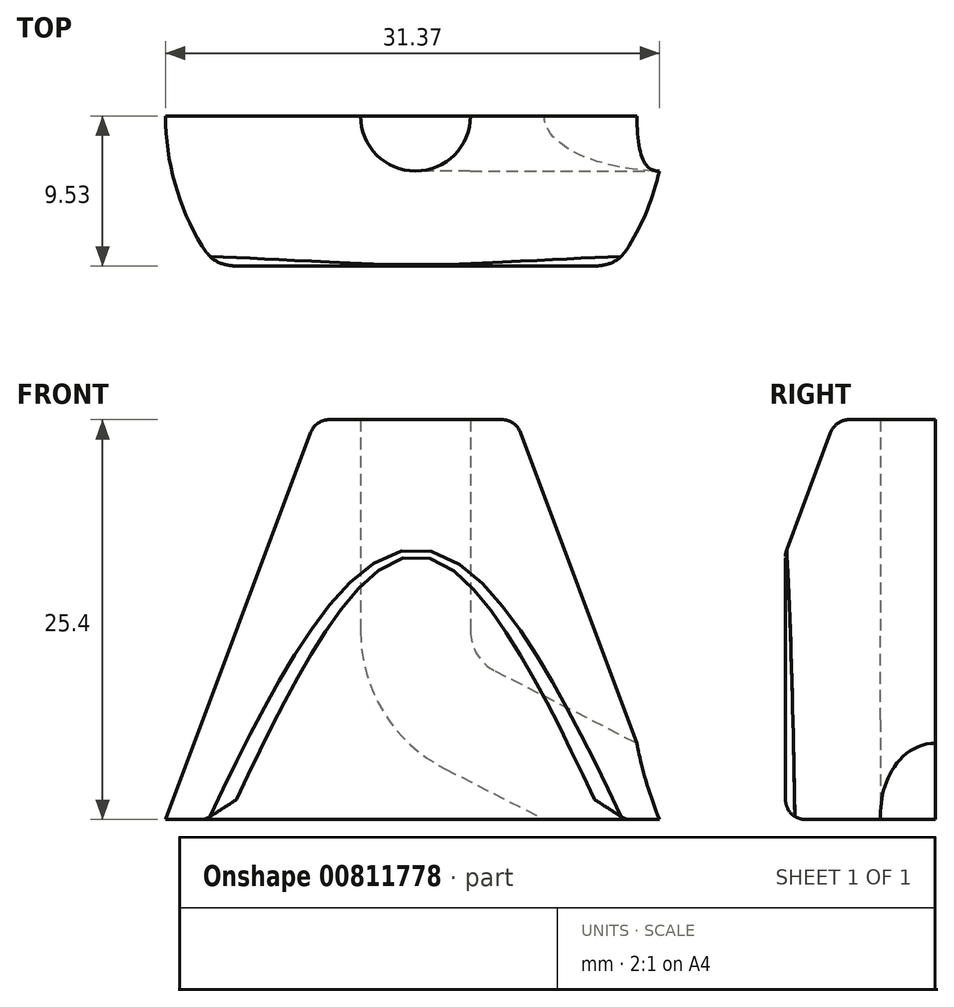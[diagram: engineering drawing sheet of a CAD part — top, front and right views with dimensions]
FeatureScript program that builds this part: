
annotation { "Feature Type Name" : "Feature", "Feature Type Description" : "" }
export const myFeature = defineFeature(function(context is Context, id is Id, definition is map)
    precondition{}
    {
        {
            var Q0;
            Q0=qCreatedBy(makeId("Front.planeOp"),FACE);
            var sketch = newSketch(context, id + "F0", { "sketchPlane" : qUnion([Q0])});
            skCircle(sketch, "E0", {"center": v(0, 0) * mm, "radius": 6.35 * mm});
            skSolve(sketch);
        }
        {
            var Q0;
            Q0=qCreatedBy(makeId("Front.planeOp"),FACE);
            cPlane(context, id + "F1", {"entities" : qUnion([Q0]), "cplaneType" : CPlaneType.OFFSET, "offset" : 25.4 * mm, "width" : 152.4 * mm, "height" : 152.4 * mm});
        }
        {
            var Q0;
            Q0=qCreatedBy(id+"F1.planeOp",FACE);
            var sketch = newSketch(context, id + "F2", { "sketchPlane" : qUnion([Q0])});
            skCircle(sketch, "E1", {"center": v(0, 0) * mm, "radius": 15.88 * mm});
            skSolve(sketch);
        }
        {
            var Q0;
            Q0=qSketchRegion(id+"F0",true);
            var Q1;
            Q1=qSketchRegion(id+"F2",true);
            loft(context, id + "F3", {"sheetProfilesArray" : [{ "sheetProfileEntities" : qUnion([Q0]) }, { "sheetProfileEntities" : qUnion([Q1]) }]});
        }
        {
            var Q0;
            Q0=qCreatedBy(makeId("Top.planeOp"),FACE);
            cPlane(context, id + "F4", {"entities" : qUnion([Q0]), "cplaneType" : CPlaneType.OFFSET, "offset" : 9.52 * mm, "width" : 152.4 * mm, "height" : 152.4 * mm});
        }
        {
            var Q0;
            Q0=qCreatedBy(id+"F4.planeOp",FACE);
            var sketch = newSketch(context, id + "F5", { "sketchPlane" : qUnion([Q0])});
            skCircle(sketch, "E2", {"center": v(0, 0) * mm, "radius": 36.69 * mm});
            skSolve(sketch);
        }
        {
            var Q0;
            Q0=qSketchRegion(id+"F5",true);
            extrude(context, id + "F6", {"entities" : qUnion([Q0]), "operationType" : NewBodyOperationType.REMOVE, "endBound" : BoundingType.THROUGH_ALL, "depth" : 25.4 * mm, "offsetDistance" : 25.4 * mm});
        }
        {
            var Q0;
            Q0=qCreatedBy(makeId("Top.planeOp"),FACE);
            var sketch = newSketch(context, id + "F7", { "sketchPlane" : qUnion([Q0])});
            skCircle(sketch, "E3", {"center": v(0, 0) * mm, "radius": 33.8 * mm});
            skSolve(sketch);
        }
        {
            var Q0;
            Q0=qSketchRegion(id+"F7",true);
            extrude(context, id + "F8", {"entities" : qUnion([Q0]), "operationType" : NewBodyOperationType.REMOVE, "oppositeDirection" : true, "depth" : 25.4 * mm, "offsetDistance" : 25.4 * mm});
        }
        {
            var Q0;
            Q0=makeQuery(id+"F3.opLoft","MID_CAP_EDGE",EDGE,{"disambiguationData":[OSD([sQuery(id+"F0.wireOp",EDGE,"E0")])],"capPos":0.0});
            fillet(context, id + "F9", {"entities" : qUnion([Q0]), "radius" : 1.27 * mm, "tangentPropagation" : true, "allowEdgeOverflow" : false});
        }
        {
            var Q0;
            Q0=makeQuery(id+"F3.opLoft","SWEPT_BODY",BODY,{"disambiguationData":[OSD([makeQuery(id+"F0.imprint","IMPRINT",FACE,{"disambiguationData":[TD([[makeQuery(id+"F0.imprint","IMPRINT",EDGE,{"derivedFrom":sQuery(id+"F0.wireOp",EDGE,"E0")}),1.0]])]}),makeQuery(id+"F2.imprint","IMPRINT",FACE,{"disambiguationData":[TD([[makeQuery(id+"F2.imprint","IMPRINT",EDGE,{"derivedFrom":sQuery(id+"F2.wireOp",EDGE,"E1")}),1.0]])]})])]});
            var Q1;
            Q1=makeQuery(id+"F8.boolean.opBoolean","INTERSECT",EDGE,{"disambiguationData":[OD(0.0)],"derivedFrom":[makeQuery(id+"F3.opLoft","CAP_FACE",FACE,{"disambiguationData":[OSD([makeQuery(id+"F2.imprint","IMPRINT",FACE,{"disambiguationData":[TD([[makeQuery(id+"F2.imprint","IMPRINT",EDGE,{"derivedFrom":sQuery(id+"F2.wireOp",EDGE,"E1")}),1.0]])]})])],"isStart":true}),makeQuery(id+"F8.opExtrude","CAP_FACE",FACE,{"disambiguationData":[OSD([sQuery(id+"F7.wireOp",EDGE,"E3")])],"isStart":true})]});
            transform(context, id + "F10", {"entities" : qUnion([Q0]), "transformType" : TransformType.ROTATION, "transformAxis" : qUnion([Q1]), "angle" : 90 * degree, "oppositeDirection" : true, "makeCopy" : false});
        }
        {
            var Q0;
            Q0=makeQuery(id+"F6.boolean.opBoolean","COPY",FACE,{"derivedFrom":makeQuery(id+"F6.opExtrude","CAP_FACE",FACE,{"disambiguationData":[OSD([sQuery(id+"F5.wireOp",EDGE,"E2")])],"isStart":true})});
            fillet(context, id + "F11", {"entities" : qUnion([Q0]), "radius" : 1.27 * mm, "tangentPropagation" : true, "allowEdgeOverflow" : false});
        }
        {
            var Q0;
            Q0=makeQuery(id+"F8.boolean.opBoolean","COPY",FACE,{"derivedFrom":makeQuery(id+"F8.opExtrude","CAP_FACE",FACE,{"disambiguationData":[OSD([sQuery(id+"F7.wireOp",EDGE,"E3")])],"isStart":true})});
            var sketch = newSketch(context, id + "F12", { "sketchPlane" : qUnion([Q0])});
            skLineSegment(sketch, "E4", {"start": v(0, 25.4) * mm, "end": v(0, 11.98) * mm});
            skLineSegment(sketch, "E5", {"start": v(-3.47, 6.32) * mm, "end": v(-15.88, 0) * mm});
            skPoint(sketch, "E6.visualSharp", {"position": v(0, 8.09) * mm});
            skArc(sketch, "E6.filletArc", {"start": v(-3.47, 6.32) * mm, "mid": v(-0.94, 8.66) * mm, "end": v(0, 11.98) * mm});
            skSolve(sketch);
        }
        {
            var Q0;
            Q0=makeQuery(id+"F3.opLoft","CAP_FACE",FACE,{"disambiguationData":[OSD([makeQuery(id+"F0.imprint","IMPRINT",FACE,{"disambiguationData":[TD([[makeQuery(id+"F0.imprint","IMPRINT",EDGE,{"derivedFrom":sQuery(id+"F0.wireOp",EDGE,"E0")}),1.0]])]})])],"isStart":true});
            var sketch = newSketch(context, id + "F13", { "sketchPlane" : qUnion([Q0])});
            skCircle(sketch, "E7", {"center": v(0, -25.4) * mm, "radius": 3.5 * mm});
            skSolve(sketch);
        }
        {
            var Q0;
            Q0=qSketchRegion(id+"F13",true);
            var Q1;
            Q1=qConstructionFilter(qBodyType(qCreatedBy(id+"F12",EDGE),BodyType.WIRE),ConstructionObject.NO);
            sweep(context, id + "F14", {"operationType" : NewBodyOperationType.REMOVE, "profiles" : qUnion([Q0]), "path" : qUnion([Q1])});
        }
    });
